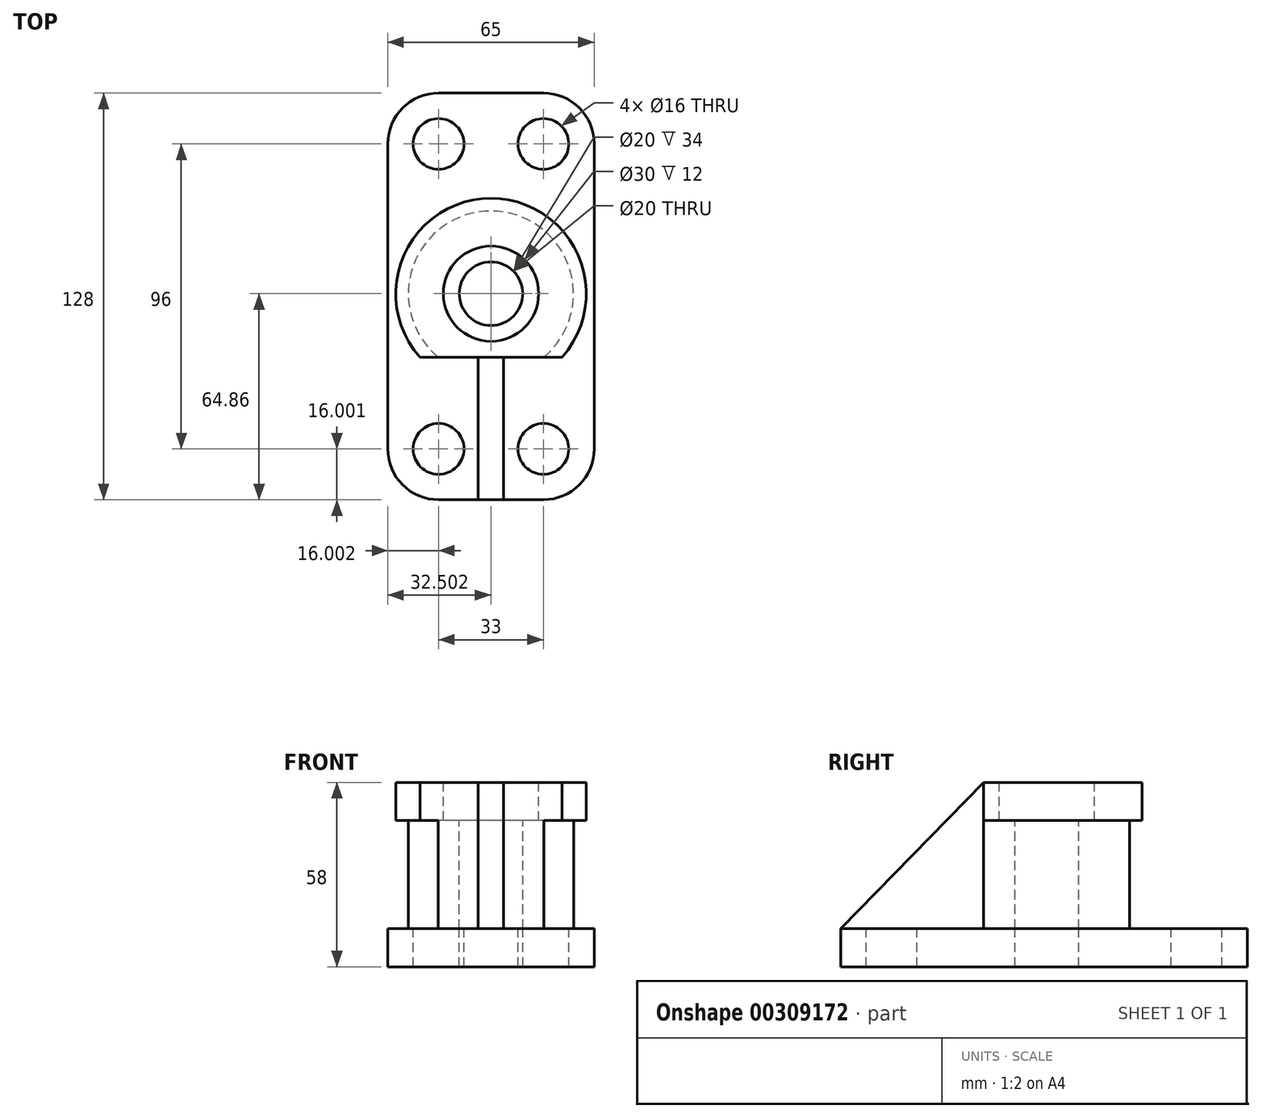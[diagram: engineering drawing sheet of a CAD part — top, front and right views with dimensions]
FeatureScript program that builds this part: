
annotation { "Feature Type Name" : "Feature", "Feature Type Description" : "" }
export const myFeature = defineFeature(function(context is Context, id is Id, definition is map)
    precondition{}
    {
        {
            var Q0;
            Q0=qCreatedBy(makeId("Top.planeOp"),FACE);
            var sketch = newSketch(context, id + "F0", { "sketchPlane" : qUnion([Q0])});
            skLineSegment(sketch, "E0", {"start": v(-47.28, 47.14) * mm, "end": v(-47.28, -48.86) * mm});
            skLineSegment(sketch, "E1", {"start": v(-31.28, -64.86) * mm, "end": v(1.72, -64.86) * mm});
            skLineSegment(sketch, "E2", {"start": v(17.72, -48.86) * mm, "end": v(17.72, 47.14) * mm});
            skLineSegment(sketch, "E3", {"start": v(1.72, 63.14) * mm, "end": v(-31.28, 63.14) * mm});
            skPoint(sketch, "E4.centerSnap0", {"position": v(-14.78, 63.14) * mm});
            skPoint(sketch, "E5.visualSharp", {"position": v(17.72, 63.14) * mm});
            skArc(sketch, "E5.filletArc", {"start": v(17.72, 47.14) * mm, "mid": v(13.04, 58.45) * mm, "end": v(1.72, 63.14) * mm});
            skPoint(sketch, "E6.visualSharp", {"position": v(-47.28, 63.14) * mm});
            skArc(sketch, "E6.filletArc", {"start": v(-31.28, 63.14) * mm, "mid": v(-42.6, 58.45) * mm, "end": v(-47.28, 47.14) * mm});
            skPoint(sketch, "E7.visualSharp", {"position": v(-47.28, -64.86) * mm});
            skArc(sketch, "E7.filletArc", {"start": v(-47.28, -48.86) * mm, "mid": v(-42.6, -60.17) * mm, "end": v(-31.28, -64.86) * mm});
            skPoint(sketch, "E8.visualSharp", {"position": v(17.72, -64.86) * mm});
            skArc(sketch, "E8.filletArc", {"start": v(1.72, -64.86) * mm, "mid": v(13.04, -60.17) * mm, "end": v(17.72, -48.86) * mm});
            skSolve(sketch);
        }
        {
            var Q0;
            Q0=makeQuery(id+"F0.imprint","IMPRINT",FACE,{"disambiguationData":[TD([[makeQuery(id+"F0.imprint","IMPRINT",EDGE,{"derivedFrom":sQuery(id+"F0.wireOp",EDGE,"E0")}),1.0]])]});
            extrude(context, id + "F1", {"entities" : qUnion([Q0]), "depth" : 12 * mm});
        }
        {
            var Q0;
            Q0=makeQuery(id+"F1.opExtrude","CAP_FACE",FACE,{"disambiguationData":[OSD([sQuery(id+"F0.wireOp",EDGE,"E0"),sQuery(id+"F0.wireOp",EDGE,"E1"),sQuery(id+"F0.wireOp",EDGE,"E2"),sQuery(id+"F0.wireOp",EDGE,"E3"),sQuery(id+"F0.wireOp",EDGE,"E5.filletArc"),sQuery(id+"F0.wireOp",EDGE,"E6.filletArc"),sQuery(id+"F0.wireOp",EDGE,"E7.filletArc"),sQuery(id+"F0.wireOp",EDGE,"E8.filletArc")])],"isStart":false});
            var sketch = newSketch(context, id + "F2", { "sketchPlane" : qUnion([Q0])});
            skCircle(sketch, "E9", {"center": v(-31.28, 47.14) * mm, "radius": 8 * mm});
            skCircle(sketch, "E10", {"center": v(1.72, 47.14) * mm, "radius": 8 * mm});
            skCircle(sketch, "E11", {"center": v(1.72, -48.86) * mm, "radius": 8 * mm});
            skCircle(sketch, "E12", {"center": v(-31.28, -48.86) * mm, "radius": 8 * mm});
            skLineSegment(sketch, "E13", {"start": v(-14.78, 63.14) * mm, "end": v(-14.78, -77.25) * mm, "construction": true});
            skPoint(sketch, "E13.endSnap0", {"position": v(-14.78, 63.14) * mm});
            skSolve(sketch);
        }
        {
            var Q0;
            Q0=makeQuery(id+"F2.imprint","IMPRINT",FACE,{"disambiguationData":[TD([[makeQuery(id+"F2.imprint","IMPRINT",EDGE,{"derivedFrom":sQuery(id+"F2.wireOp",EDGE,"E9")}),1.0]])]});
            var Q1;
            Q1=makeQuery(id+"F2.imprint","IMPRINT",FACE,{"disambiguationData":[TD([[makeQuery(id+"F2.imprint","IMPRINT",EDGE,{"derivedFrom":sQuery(id+"F2.wireOp",EDGE,"E10")}),1.0]])]});
            var Q2;
            Q2=makeQuery(id+"F2.imprint","IMPRINT",FACE,{"disambiguationData":[TD([[makeQuery(id+"F2.imprint","IMPRINT",EDGE,{"derivedFrom":sQuery(id+"F2.wireOp",EDGE,"E11")}),1.0]])]});
            var Q3;
            Q3=makeQuery(id+"F2.imprint","IMPRINT",FACE,{"disambiguationData":[TD([[makeQuery(id+"F2.imprint","IMPRINT",EDGE,{"derivedFrom":sQuery(id+"F2.wireOp",EDGE,"E12")}),1.0]])]});
            extrude(context, id + "F3", {"entities" : qUnion([Q0, Q1, Q2, Q3]), "operationType" : NewBodyOperationType.REMOVE, "oppositeDirection" : true, "depth" : 25 * mm});
        }
        {
            var Q0;
            Q0=makeQuery(id+"F1.opExtrude","CAP_FACE",FACE,{"disambiguationData":[OSD([sQuery(id+"F0.wireOp",EDGE,"E0"),sQuery(id+"F0.wireOp",EDGE,"E1"),sQuery(id+"F0.wireOp",EDGE,"E2"),sQuery(id+"F0.wireOp",EDGE,"E3"),sQuery(id+"F0.wireOp",EDGE,"E5.filletArc"),sQuery(id+"F0.wireOp",EDGE,"E6.filletArc"),sQuery(id+"F0.wireOp",EDGE,"E7.filletArc"),sQuery(id+"F0.wireOp",EDGE,"E8.filletArc")])],"isStart":false});
            var sketch = newSketch(context, id + "F4", { "sketchPlane" : qUnion([Q0])});
            skCircle(sketch, "E14", {"center": v(-14.78, 0) * mm, "radius": 26 * mm});
            skPoint(sketch, "E14.centerSnap0", {"position": v(-14.78, 63.14) * mm});
            skSolve(sketch);
        }
        {
            var Q0;
            Q0=makeQuery(id+"F4.imprint","IMPRINT",FACE,{"disambiguationData":[TD([[makeQuery(id+"F4.imprint","IMPRINT",EDGE,{"derivedFrom":sQuery(id+"F4.wireOp",EDGE,"E14")}),1.0]])]});
            extrude(context, id + "F5", {"entities" : qUnion([Q0]), "depth" : 46 * mm});
        }
        {
            var Q0;
            Q0=makeQuery(id+"F5.opExtrude","CAP_FACE",FACE,{"disambiguationData":[OSD([sQuery(id+"F4.wireOp",EDGE,"E14")])],"isStart":false});
            var sketch = newSketch(context, id + "F6", { "sketchPlane" : qUnion([Q0])});
            skCircle(sketch, "E15", {"center": v(-14.78, 0) * mm, "radius": 10 * mm});
            skSolve(sketch);
        }
        {
            var Q0;
            Q0=makeQuery(id+"F6.imprint","IMPRINT",FACE,{"disambiguationData":[TD([[makeQuery(id+"F6.imprint","IMPRINT",EDGE,{"derivedFrom":sQuery(id+"F6.wireOp",EDGE,"E15")}),1.0]])]});
            extrude(context, id + "F7", {"entities" : qUnion([Q0]), "operationType" : NewBodyOperationType.REMOVE, "oppositeDirection" : true, "depth" : 58 * mm});
        }
        {
            var Q0;
            Q0=makeQuery(id+"F5.opExtrude","CAP_FACE",FACE,{"disambiguationData":[OSD([sQuery(id+"F4.wireOp",EDGE,"E14")])],"isStart":false});
            var sketch = newSketch(context, id + "F8", { "sketchPlane" : qUnion([Q0])});
            skCircle(sketch, "E16", {"center": v(-14.78, 0) * mm, "radius": 30 * mm});
            skSolve(sketch);
        }
        {
            var Q0;
            Q0 = qSketchRegion(id + "F8", true);
            extrude(context, id + "F9", {"entities" : qUnion([Q0]), "operationType" : NewBodyOperationType.ADD, "oppositeDirection" : true, "depth" : 12 * mm});
        }
        {
            var Q0;
            Q0=makeQuery(id+"F9.boolean.opBoolean","MERGE",FACE,{"derivedFrom":[makeQuery(id+"F5.opExtrude","CAP_FACE",FACE,{"disambiguationData":[OSD([sQuery(id+"F4.wireOp",EDGE,"E14")])],"isStart":false}),makeQuery(id+"F9.opExtrude","CAP_FACE",FACE,{"disambiguationData":[OSD([sQuery(id+"F8.wireOp",EDGE,"E16")])],"isStart":true})]});
            var sketch = newSketch(context, id + "F10", { "sketchPlane" : qUnion([Q0])});
            skCircle(sketch, "E17", {"center": v(-14.78, 0) * mm, "radius": 15 * mm});
            skSolve(sketch);
        }
        {
            var Q0;
            Q0=makeQuery(id+"F10.imprint","IMPRINT",FACE,{"disambiguationData":[TD([[makeQuery(id+"F10.imprint","IMPRINT",EDGE,{"derivedFrom":sQuery(id+"F10.wireOp",EDGE,"E17")}),1.0]])]});
            extrude(context, id + "F11", {"entities" : qUnion([Q0]), "operationType" : NewBodyOperationType.REMOVE, "oppositeDirection" : true, "depth" : 12 * mm});
        }
        {
            var Q0;
            Q0=makeQuery(id+"F9.boolean.opBoolean","MERGE",FACE,{"derivedFrom":[makeQuery(id+"F5.opExtrude","CAP_FACE",FACE,{"disambiguationData":[OSD([sQuery(id+"F4.wireOp",EDGE,"E14")])],"isStart":false}),makeQuery(id+"F9.opExtrude","CAP_FACE",FACE,{"disambiguationData":[OSD([sQuery(id+"F8.wireOp",EDGE,"E16")])],"isStart":true})]});
            var sketch = newSketch(context, id + "F12", { "sketchPlane" : qUnion([Q0])});
            skLineSegment(sketch, "E18", {"start": v(-44.78, 0) * mm, "end": v(39.69, 0) * mm, "construction": true});
            skLineSegment(sketch, "E19.0", {"start": v(-44.78, -20) * mm, "end": v(39.69, -20) * mm});
            skSolve(sketch);
        }
        {
            var Q0;
            {var subQ0=sQuery(id+"F12.wireOp",EDGE,"E19.0");var subQ1=makeQuery(id+"F9.opExtrude","CAP_EDGE",EDGE,{"disambiguationData":[OSD([sQuery(id+"F8.wireOp",EDGE,"E16")])],"isStart":true});var subQ2=makeQuery(id+"F12.imprint","INTERSECT",VERTEX,{"disambiguationData":[OD(0.0)],"derivedFrom":[subQ1,subQ0]});Q0=makeQuery(id+"F12.imprint","IMPRINT",FACE,{"disambiguationData":[TD([[makeQuery(id+"F12.imprint","IMPRINT",EDGE,{"disambiguationData":[TD([[subQ2,-1.0]])],"derivedFrom":subQ0}),-1.0]])]});}
            var Q1;
            Q1=makeQuery(id+"F1.opExtrude","CAP_FACE",FACE,{"disambiguationData":[OSD([sQuery(id+"F0.wireOp",EDGE,"E0"),sQuery(id+"F0.wireOp",EDGE,"E1"),sQuery(id+"F0.wireOp",EDGE,"E2"),sQuery(id+"F0.wireOp",EDGE,"E3"),sQuery(id+"F0.wireOp",EDGE,"E5.filletArc"),sQuery(id+"F0.wireOp",EDGE,"E6.filletArc"),sQuery(id+"F0.wireOp",EDGE,"E7.filletArc"),sQuery(id+"F0.wireOp",EDGE,"E8.filletArc")])],"isStart":false});
            extrude(context, id + "F13", {"entities" : qUnion([Q0]), "operationType" : NewBodyOperationType.REMOVE, "endBound" : BoundingType.UP_TO_SURFACE, "oppositeDirection" : true, "endBoundEntityFace" : qUnion([Q1]), "depth" : 25 * mm});
        }
        {
            var Q0;
            Q0=makeQuery(id+"F1.opExtrude","CAP_FACE",FACE,{"disambiguationData":[OSD([sQuery(id+"F0.wireOp",EDGE,"E0"),sQuery(id+"F0.wireOp",EDGE,"E1"),sQuery(id+"F0.wireOp",EDGE,"E2"),sQuery(id+"F0.wireOp",EDGE,"E3"),sQuery(id+"F0.wireOp",EDGE,"E5.filletArc"),sQuery(id+"F0.wireOp",EDGE,"E6.filletArc"),sQuery(id+"F0.wireOp",EDGE,"E7.filletArc"),sQuery(id+"F0.wireOp",EDGE,"E8.filletArc")])],"isStart":false});
            var sketch = newSketch(context, id + "F14", { "sketchPlane" : qUnion([Q0])});
            skLineSegment(sketch, "E20", {"start": v(-18.78, -64.86) * mm, "end": v(-10.78, -64.86) * mm});
            skPoint(sketch, "E21.endSnap0", {"position": v(-14.78, -64.86) * mm});
            skLineSegment(sketch, "E22", {"start": v(-14.78, -64.86) * mm, "end": v(-14.78, -20) * mm, "construction": true});
            skLineSegment(sketch, "E23", {"start": v(-14.78, -20) * mm, "end": v(-10.78, -20) * mm});
            skLineSegment(sketch, "E24", {"start": v(-10.78, -20) * mm, "end": v(-10.78, -64.86) * mm});
            skLineSegment(sketch, "E25", {"start": v(-18.78, -20) * mm, "end": v(-14.78, -20) * mm});
            skLineSegment(sketch, "E26", {"start": v(-18.78, -20) * mm, "end": v(-18.78, -64.86) * mm});
            skSolve(sketch);
        }
        {
            var Q0;
            Q0=makeQuery(id+"F14.imprint","IMPRINT",FACE,{"disambiguationData":[TD([[makeQuery(id+"F14.imprint","IMPRINT",EDGE,{"derivedFrom":sQuery(id+"F14.wireOp",EDGE,"E20")}),1.0]])]});
            extrude(context, id + "F15", {"entities" : qUnion([Q0]), "depth" : 46 * mm});
        }
        {
            var Q0;
            Q0=makeQuery(id+"F15.opExtrude","SWEPT_FACE",FACE,{"disambiguationData":[OSD([sQuery(id+"F14.wireOp",EDGE,"E24")])]});
            var sketch = newSketch(context, id + "F16", { "sketchPlane" : qUnion([Q0])});
            skLineSegment(sketch, "E27", {"start": v(-20, 58) * mm, "end": v(-64.86, 12) * mm});
            skLineSegment(sketch, "E28", {"start": v(-64.86, 12) * mm, "end": v(-20, 12) * mm});
            skLineSegment(sketch, "E29", {"start": v(-20, 12) * mm, "end": v(-20, 58) * mm});
            skSolve(sketch);
        }
        {
            var Q0;
            Q0=makeQuery(id+"F16.imprint","IMPRINT",FACE,{"disambiguationData":[TD([[makeQuery(id+"F16.imprint","IMPRINT",EDGE,{"derivedFrom":sQuery(id+"F16.wireOp",EDGE,"E27")}),-1.0]])]});
            extrude(context, id + "F17", {"entities" : qUnion([Q0]), "operationType" : NewBodyOperationType.REMOVE, "oppositeDirection" : true, "depth" : 8 * mm});
        }
    });
